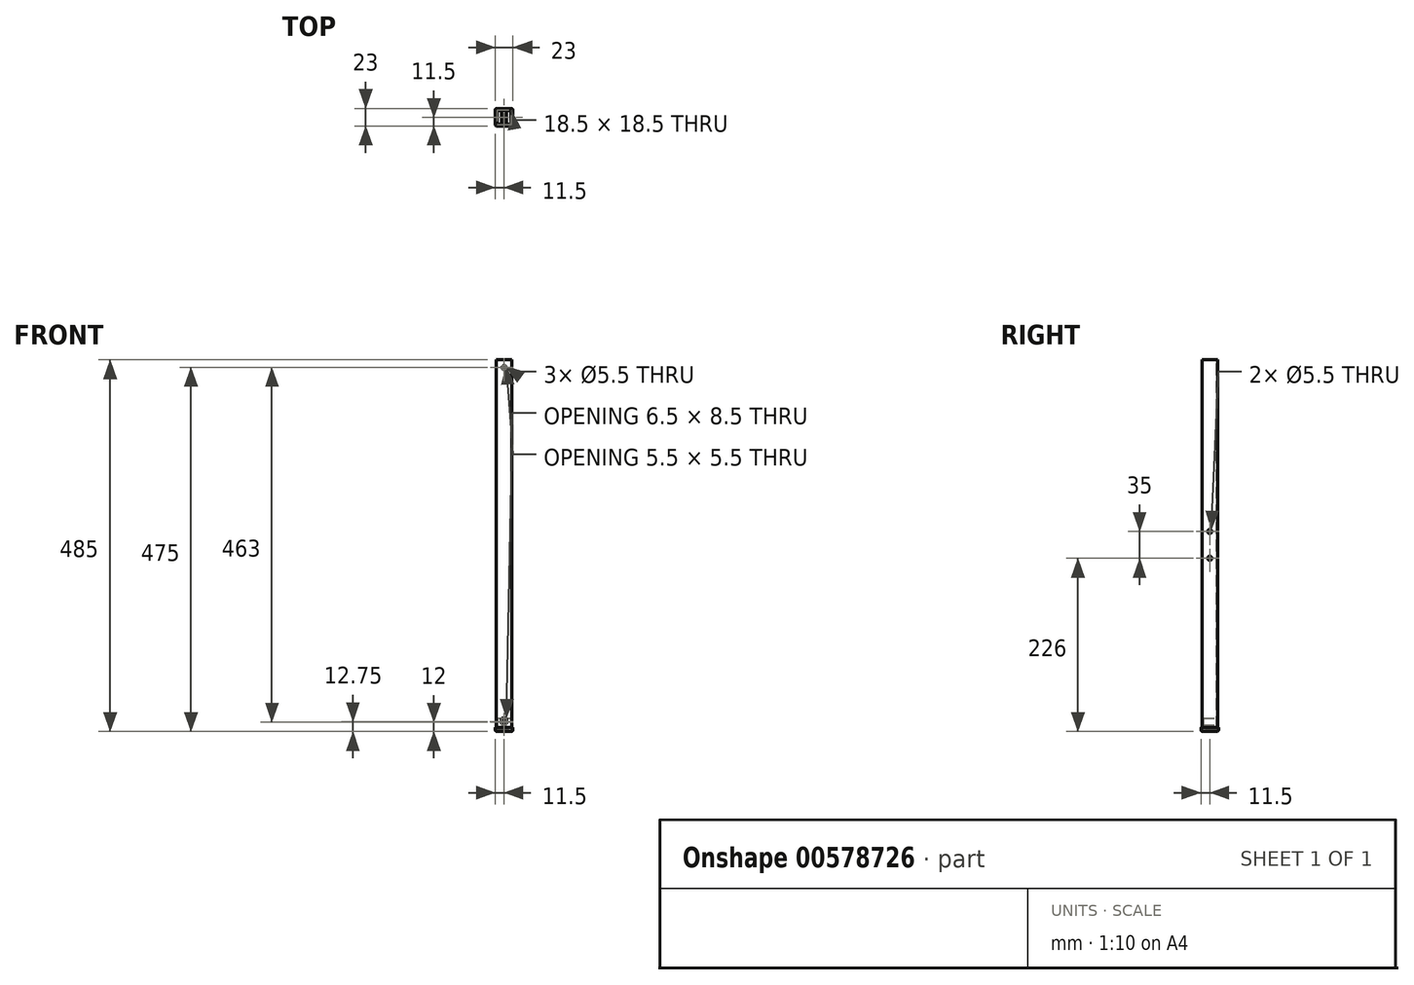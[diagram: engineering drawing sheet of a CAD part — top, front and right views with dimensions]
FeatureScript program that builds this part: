
annotation { "Feature Type Name" : "Feature", "Feature Type Description" : "" }
export const myFeature = defineFeature(function(context is Context, id is Id, definition is map)
    precondition{}
    {
        {
            var Q0;
            Q0=qCreatedBy(makeId("Top.planeOp"),FACE);
            var sketch = newSketch(context, id + "F0", { "sketchPlane" : qUnion([Q0])});
            skLineSegment(sketch, "E0.bottom", {"start": v(-10, 10) * mm, "end": v(10, 10) * mm});
            skLineSegment(sketch, "E0.top", {"start": v(-10, -10) * mm, "end": v(10, -10) * mm});
            skLineSegment(sketch, "E0.left", {"start": v(-10, 10) * mm, "end": v(-10, -10) * mm});
            skLineSegment(sketch, "E0.right", {"start": v(10, 10) * mm, "end": v(10, -10) * mm});
            skSolve(sketch);
        }
        {
            var Q0;
            Q0 = qSketchRegion(id + "F0", true);
            extrude(context, id + "F1", {"entities" : qUnion([Q0]), "depth" : 483 * mm, "offsetDistance" : 25 * mm});
        }
        {
            var Q0;
            Q0=makeQuery(id+"F1.opExtrude","CAP_FACE",FACE,{"disambiguationData":[OSD([sQuery(id+"F0.wireOp",EDGE,"E0.bottom"),sQuery(id+"F0.wireOp",EDGE,"E0.top"),sQuery(id+"F0.wireOp",EDGE,"E0.left"),sQuery(id+"F0.wireOp",EDGE,"E0.right")])],"isStart":false});
            var sketch = newSketch(context, id + "F2", { "sketchPlane" : qUnion([Q0])});
            skLineSegment(sketch, "E1.bottom", {"start": v(-9.25, 9.25) * mm, "end": v(9.25, 9.25) * mm});
            skLineSegment(sketch, "E1.top", {"start": v(-9.25, -9.25) * mm, "end": v(9.25, -9.25) * mm});
            skLineSegment(sketch, "E1.left", {"start": v(-9.25, 9.25) * mm, "end": v(-9.25, -9.25) * mm});
            skLineSegment(sketch, "E1.right", {"start": v(9.25, 9.25) * mm, "end": v(9.25, -9.25) * mm});
            skSolve(sketch);
        }
        {
            var Q0;
            Q0 = qSketchRegion(id + "F2", true);
            extrude(context, id + "F3", {"entities" : qUnion([Q0]), "operationType" : NewBodyOperationType.REMOVE, "endBound" : BoundingType.THROUGH_ALL, "oppositeDirection" : true, "depth" : 25 * mm, "offsetDistance" : 25 * mm});
        }
        {
            var Q0;
            Q0=makeQuery(id+"F1.opExtrude","SWEPT_FACE",FACE,{"disambiguationData":[OSD([sQuery(id+"F0.wireOp",EDGE,"E0.bottom")])]});
            var sketch = newSketch(context, id + "F4", { "sketchPlane" : qUnion([Q0])});
            skCircle(sketch, "E2", {"center": v(0, 473) * mm, "radius": 2.75 * mm});
            skCircle(sketch, "E3", {"center": v(0, 10) * mm, "radius": 2.75 * mm});
            skSolve(sketch);
        }
        {
            var Q0;
            Q0 = qSketchRegion(id + "F4", true);
            extrude(context, id + "F5", {"entities" : qUnion([Q0]), "operationType" : NewBodyOperationType.REMOVE, "oppositeDirection" : true, "depth" : 25 * mm, "offsetDistance" : 25 * mm});
        }
        {
            var Q0;
            Q0=qCreatedBy(makeId("Top.planeOp"),FACE);
            cPlane(context, id + "F6", {"entities" : qUnion([Q0]), "cplaneType" : CPlaneType.OFFSET, "offset" : 2 * mm, "oppositeDirection" : true, "width" : 150 * mm, "height" : 150 * mm});
        }
        {
            var Q0;
            Q0=qCreatedBy(id+"F6.planeOp",FACE);
            var sketch = newSketch(context, id + "F7", { "sketchPlane" : qUnion([Q0])});
            skLineSegment(sketch, "E4.bottom", {"start": v(-11.5, -11.5) * mm, "end": v(11.5, -11.5) * mm});
            skLineSegment(sketch, "E4.top", {"start": v(-11.5, 11.5) * mm, "end": v(11.5, 11.5) * mm});
            skLineSegment(sketch, "E4.left", {"start": v(-11.5, -11.5) * mm, "end": v(-11.5, 11.5) * mm});
            skLineSegment(sketch, "E4.right", {"start": v(11.5, -11.5) * mm, "end": v(11.5, 11.5) * mm});
            skSolve(sketch);
        }
        {
            var Q0;
            Q0 = qSketchRegion(id + "F7", true);
            extrude(context, id + "F8", {"entities" : qUnion([Q0]), "depth" : 5 * mm, "offsetDistance" : 25 * mm});
        }
        {
            var Q0;
            Q0=makeQuery(id+"F8.opExtrude","CAP_FACE",FACE,{"disambiguationData":[OSD([sQuery(id+"F7.wireOp",EDGE,"E4.bottom"),sQuery(id+"F7.wireOp",EDGE,"E4.top"),sQuery(id+"F7.wireOp",EDGE,"E4.left"),sQuery(id+"F7.wireOp",EDGE,"E4.right")])],"isStart":false});
            var sketch = newSketch(context, id + "F9", { "sketchPlane" : qUnion([Q0])});
            skLineSegment(sketch, "E5.bottom", {"start": v(-10.25, 10.25) * mm, "end": v(10.25, 10.25) * mm});
            skLineSegment(sketch, "E5.top", {"start": v(-10.25, -10.25) * mm, "end": v(10.25, -10.25) * mm});
            skLineSegment(sketch, "E5.left", {"start": v(-10.25, 10.25) * mm, "end": v(-10.25, -10.25) * mm});
            skLineSegment(sketch, "E5.right", {"start": v(10.25, 10.25) * mm, "end": v(10.25, -10.25) * mm});
            skSolve(sketch);
        }
        {
            var Q0;
            Q0 = qSketchRegion(id + "F9", true);
            extrude(context, id + "F10", {"entities" : qUnion([Q0]), "operationType" : NewBodyOperationType.REMOVE, "oppositeDirection" : true, "depth" : 3 * mm, "offsetDistance" : 25 * mm});
        }
        {
            var Q0;
            Q0=makeQuery(id+"F10.boolean.opBoolean","COPY",FACE,{"derivedFrom":makeQuery(id+"F10.opExtrude","CAP_FACE",FACE,{"disambiguationData":[OSD([sQuery(id+"F9.wireOp",EDGE,"E5.bottom"),sQuery(id+"F9.wireOp",EDGE,"E5.top"),sQuery(id+"F9.wireOp",EDGE,"E5.left"),sQuery(id+"F9.wireOp",EDGE,"E5.right")])],"isStart":false})});
            var sketch = newSketch(context, id + "F11", { "sketchPlane" : qUnion([Q0])});
            skLineSegment(sketch, "E6.bottom", {"start": v(-9, 9) * mm, "end": v(9, 9) * mm});
            skLineSegment(sketch, "E6.top", {"start": v(-9, -9) * mm, "end": v(9, -9) * mm});
            skLineSegment(sketch, "E6.left", {"start": v(-9, 9) * mm, "end": v(-9, -9) * mm});
            skLineSegment(sketch, "E6.right", {"start": v(9, 9) * mm, "end": v(9, -9) * mm});
            skSolve(sketch);
        }
        {
            var Q0;
            Q0 = qSketchRegion(id + "F11", true);
            extrude(context, id + "F12", {"entities" : qUnion([Q0]), "operationType" : NewBodyOperationType.ADD, "depth" : 15 * mm, "offsetDistance" : 25 * mm});
        }
        {
            var Q0;
            Q0=makeQuery(id+"F12.opExtrude","SWEPT_FACE",FACE,{"disambiguationData":[OSD([sQuery(id+"F11.wireOp",EDGE,"E6.bottom")])]});
            var sketch = newSketch(context, id + "F13", { "sketchPlane" : qUnion([Q0])});
            skLineSegment(sketch, "E7.bottom", {"start": v(-3.25, 15) * mm, "end": v(3.25, 15) * mm});
            skLineSegment(sketch, "E7.left", {"start": v(-3.25, 15) * mm, "end": v(-3.25, 9.75) * mm});
            skLineSegment(sketch, "E7.right", {"start": v(3.25, 15) * mm, "end": v(3.25, 9.75) * mm});
            skArc(sketch, "E8", {"start": v(-3.25, 9.75) * mm, "mid": v(0, 6.5) * mm, "end": v(3.25, 9.75) * mm});
            skSolve(sketch);
        }
        {
            var Q0;
            Q0 = qSketchRegion(id + "F13", true);
            extrude(context, id + "F14", {"entities" : qUnion([Q0]), "operationType" : NewBodyOperationType.REMOVE, "endBound" : BoundingType.THROUGH_ALL, "oppositeDirection" : true, "depth" : 25 * mm, "offsetDistance" : 25 * mm});
        }
        {
            var Q0;
            Q0=makeQuery(id+"F8.opExtrude","SWEPT_EDGE",EDGE,{"disambiguationData":[OSD([sQuery(id+"F7.wireOp",EDGE,"E4.bottom"),sQuery(id+"F7.wireOp",EDGE,"E4.right")])]});
            var Q1;
            Q1=makeQuery(id+"F8.opExtrude","SWEPT_EDGE",EDGE,{"disambiguationData":[OSD([sQuery(id+"F7.wireOp",EDGE,"E4.bottom"),sQuery(id+"F7.wireOp",EDGE,"E4.left")])]});
            var Q2;
            Q2=makeQuery(id+"F8.opExtrude","SWEPT_EDGE",EDGE,{"disambiguationData":[OSD([sQuery(id+"F7.wireOp",EDGE,"E4.top"),sQuery(id+"F7.wireOp",EDGE,"E4.right")])]});
            var Q3;
            Q3=makeQuery(id+"F8.opExtrude","SWEPT_EDGE",EDGE,{"disambiguationData":[OSD([sQuery(id+"F7.wireOp",EDGE,"E4.top"),sQuery(id+"F7.wireOp",EDGE,"E4.left")])]});
            var Q4;
            Q4=makeQuery(id+"F8.opExtrude","CAP_FACE",FACE,{"disambiguationData":[OSD([sQuery(id+"F7.wireOp",EDGE,"E4.bottom"),sQuery(id+"F7.wireOp",EDGE,"E4.top"),sQuery(id+"F7.wireOp",EDGE,"E4.left"),sQuery(id+"F7.wireOp",EDGE,"E4.right")])],"isStart":true});
            fillet(context, id + "F15", {"entities" : qUnion([Q0, Q1, Q2, Q3, Q4]), "radius" : 2 * mm, "tangentPropagation" : true, "allowEdgeOverflow" : false});
        }
        {
            var Q0;
            Q0=makeQuery(id+"F1.opExtrude","SWEPT_FACE",FACE,{"disambiguationData":[OSD([sQuery(id+"F0.wireOp",EDGE,"E0.right")])]});
            var sketch = newSketch(context, id + "F16", { "sketchPlane" : qUnion([Q0])});
            skCircle(sketch, "E9", {"center": v(0, 224) * mm, "radius": 2.75 * mm});
            skCircle(sketch, "E10", {"center": v(0, 259) * mm, "radius": 2.75 * mm});
            skPoint(sketch, "E10.centerSnap0", {"position": v(0, 483) * mm});
            skSolve(sketch);
        }
        {
            var Q0;
            Q0 = qSketchRegion(id + "F16", true);
            extrude(context, id + "F17", {"entities" : qUnion([Q0]), "operationType" : NewBodyOperationType.REMOVE, "oppositeDirection" : true, "depth" : 5 * mm, "offsetDistance" : 25 * mm});
        }
    });
